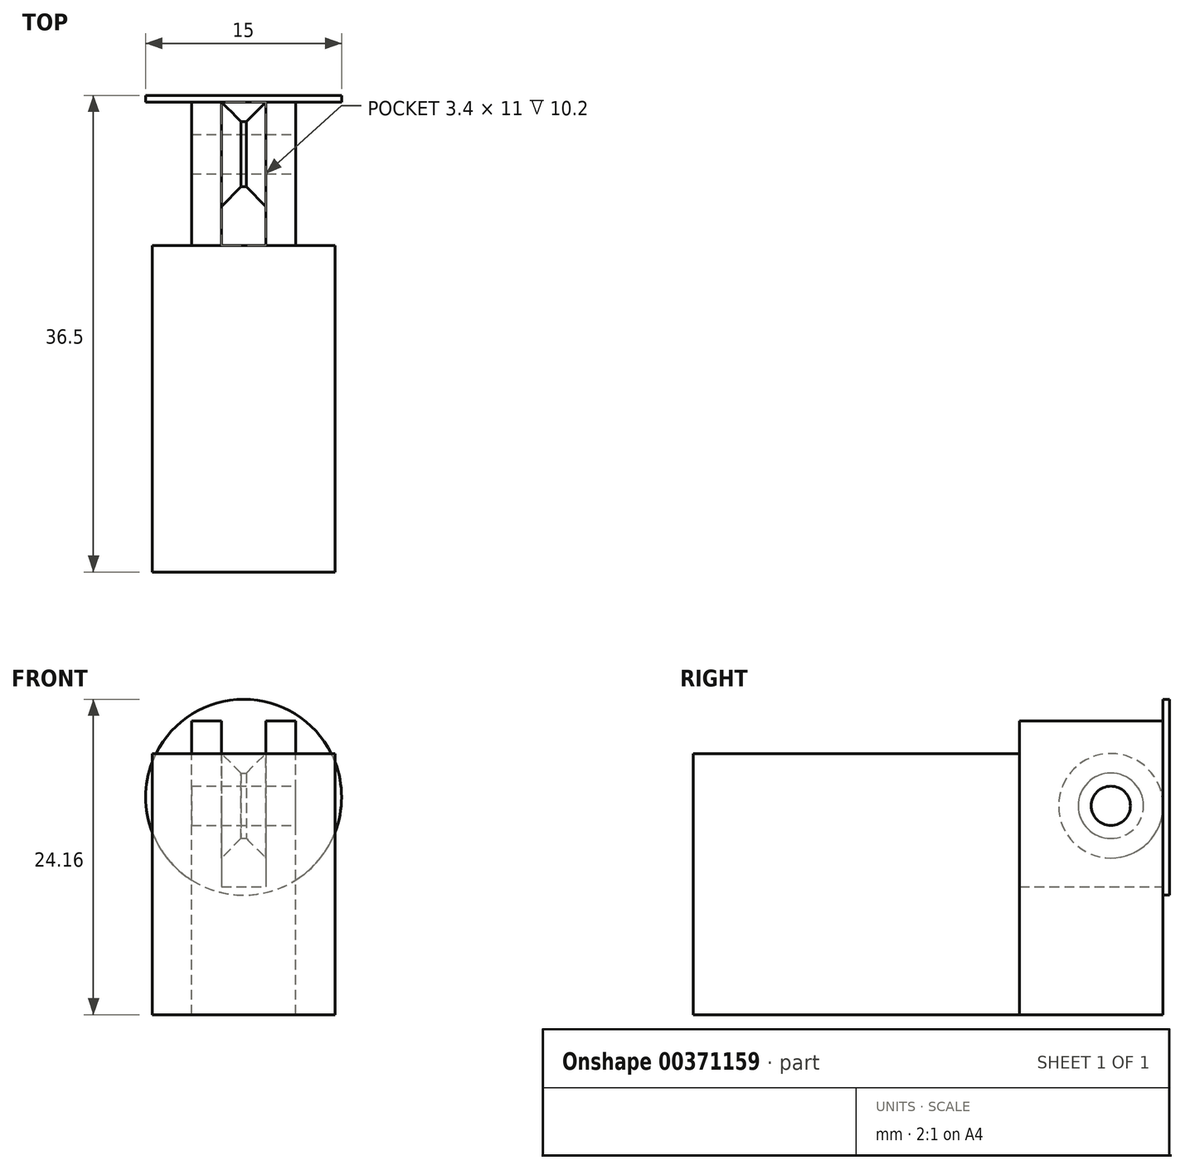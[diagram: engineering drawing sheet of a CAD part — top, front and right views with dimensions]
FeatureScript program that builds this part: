
annotation { "Feature Type Name" : "Feature", "Feature Type Description" : "" }
export const myFeature = defineFeature(function(context is Context, id is Id, definition is map)
    precondition{}
    {
        {
            var Q0;
            Q0=qCreatedBy(makeId("Front.planeOp"),FACE);
            var sketch = newSketch(context, id + "F0", { "sketchPlane" : qUnion([Q0])});
            skLineSegment(sketch, "E0", {"start": v(0, 0) * mm, "end": v(-4, 0) * mm});
            skLineSegment(sketch, "E1", {"start": v(-4, 0) * mm, "end": v(-4, 22.5) * mm});
            skLineSegment(sketch, "E2", {"start": v(-4, 22.5) * mm, "end": v(-1.7, 22.5) * mm});
            skLineSegment(sketch, "E3", {"start": v(-1.7, 22.5) * mm, "end": v(-1.7, 0) * mm, "construction": true});
            skPoint(sketch, "E3.endSnap0", {"position": v(-2, 0) * mm});
            skLineSegment(sketch, "E4", {"start": v(-1.7, 0) * mm, "end": v(-1.7, 9.8) * mm, "construction": true});
            skLineSegment(sketch, "E5", {"start": v(-1.7, 22.5) * mm, "end": v(-1.7, 9.8) * mm});
            skLineSegment(sketch, "E6", {"start": v(-1.7, 9.8) * mm, "end": v(0, 9.8) * mm});
            skLineSegment(sketch, "E7", {"start": v(0, 9.8) * mm, "end": v(0, 0) * mm});
            skCircle(sketch, "E8", {"center": v(0, 9.8) * mm, "radius": 14.4 * mm});
            skSolve(sketch);
        }
        {
            var Q0;
            Q0=makeQuery(id+"F0.imprint","IMPRINT",FACE,{"disambiguationData":[TD([[makeQuery(id+"F0.imprint","IMPRINT",EDGE,{"derivedFrom":sQuery(id+"F0.wireOp",EDGE,"E0")}),-1.0]])]});
            extrude(context, id + "F1", {"entities" : qUnion([Q0]), "depth" : 11 * mm});
        }
        {
            var Q0;
            Q0=makeQuery(id+"F1.opExtrude","SWEPT_BODY",BODY,{"disambiguationData":[OSD([sQuery(id+"F0.wireOp",EDGE,"E0"),sQuery(id+"F0.wireOp",EDGE,"E1"),sQuery(id+"F0.wireOp",EDGE,"E2"),sQuery(id+"F0.wireOp",EDGE,"E5"),sQuery(id+"F0.wireOp",EDGE,"E6"),sQuery(id+"F0.wireOp",EDGE,"E7")])]});
            var Q1;
            Q1=makeQuery(id+"F1.opExtrude","SWEPT_FACE",FACE,{"disambiguationData":[OSD([sQuery(id+"F0.wireOp",EDGE,"E7")])]});
            mirror(context, id + "F2", {"operationType" : NewBodyOperationType.ADD, "entities" : qUnion([Q0]), "mirrorPlane" : qUnion([Q1])});
        }
        {
            var Q0;
            {var subQ0=makeQuery(id+"F1.opExtrude","CAP_FACE",FACE,{"disambiguationData":[OSD([sQuery(id+"F0.wireOp",EDGE,"E0"),sQuery(id+"F0.wireOp",EDGE,"E1"),sQuery(id+"F0.wireOp",EDGE,"E2"),sQuery(id+"F0.wireOp",EDGE,"E5"),sQuery(id+"F0.wireOp",EDGE,"E6"),sQuery(id+"F0.wireOp",EDGE,"E7")])],"isStart":false});Q0=makeQuery(id+"F2.boolean.opBoolean","MERGE",FACE,{"derivedFrom":[subQ0,makeQuery(id+"F2.opPattern","COPY",FACE,{"derivedFrom":subQ0,"instanceName":"1"})]});}
            var sketch = newSketch(context, id + "F3", { "sketchPlane" : qUnion([Q0])});
            skLineSegment(sketch, "E9", {"start": v(0, 0) * mm, "end": v(-7, 0) * mm, "construction": true});
            skLineSegment(sketch, "E10", {"start": v(0, 0) * mm, "end": v(-7, 0) * mm});
            skLineSegment(sketch, "E11", {"start": v(-7, 0) * mm, "end": v(-7, 20) * mm});
            skLineSegment(sketch, "E12", {"start": v(0, 0) * mm, "end": v(7, 0) * mm});
            skLineSegment(sketch, "E13", {"start": v(7, 0) * mm, "end": v(7, 20) * mm});
            skLineSegment(sketch, "E14", {"start": v(-7, 20) * mm, "end": v(7, 20) * mm});
            skSolve(sketch);
        }
        {
            var Q0;
            {var subQ3=sQuery(id+"F3.wireOp",EDGE,"E13");Q0=makeQuery(id+"F3.imprint","IMPRINT",FACE,{"disambiguationData":[TD([[makeQuery(id+"F3.imprint","IMPRINT",EDGE,{"derivedFrom":subQ3}),1.0]])]});}
            var Q1;
            {var subQ13=makeQuery(id+"F1.opExtrude","CAP_EDGE",EDGE,{"disambiguationData":[OSD([sQuery(id+"F0.wireOp",EDGE,"E6")])],"isStart":false});var subQ14=makeQuery(id+"F2.boolean.opBoolean","MERGE",EDGE,{"derivedFrom":[subQ13,makeQuery(id+"F2.opPattern","COPY",EDGE,{"derivedFrom":subQ13,"instanceName":"1"})]});Q1=makeQuery(id+"F3.imprint","IMPRINT",FACE,{"disambiguationData":[TD([[makeQuery(id+"F3.imprint","IMPRINT",EDGE,{"derivedFrom":subQ14}),-1.0]])]});}
            var Q2;
            {var subQ5=makeQuery(id+"F1.opExtrude","CAP_EDGE",EDGE,{"disambiguationData":[OSD([sQuery(id+"F0.wireOp",EDGE,"E6")])],"isStart":false});var subQ6=makeQuery(id+"F2.boolean.opBoolean","MERGE",EDGE,{"derivedFrom":[subQ5,makeQuery(id+"F2.opPattern","COPY",EDGE,{"derivedFrom":subQ5,"instanceName":"1"})]});Q2=makeQuery(id+"F3.imprint","IMPRINT",FACE,{"disambiguationData":[TD([[makeQuery(id+"F3.imprint","IMPRINT",EDGE,{"derivedFrom":subQ6}),1.0]])]});}
            var Q3;
            {var subQ3=sQuery(id+"F3.wireOp",EDGE,"E11");Q3=makeQuery(id+"F3.imprint","IMPRINT",FACE,{"disambiguationData":[TD([[makeQuery(id+"F3.imprint","IMPRINT",EDGE,{"derivedFrom":subQ3}),-1.0]])]});}
            extrude(context, id + "F4", {"entities" : qUnion([Q0, Q1, Q2, Q3]), "operationType" : NewBodyOperationType.ADD, "depth" : 25 * mm});
        }
        {
            var Q0;
            Q0=makeQuery(id+"F2.opPattern","COPY",FACE,{"derivedFrom":makeQuery(id+"F1.opExtrude","SWEPT_FACE",FACE,{"disambiguationData":[OSD([sQuery(id+"F0.wireOp",EDGE,"E1")])]}),"instanceName":"1"});
            var sketch = newSketch(context, id + "F5", { "sketchPlane" : qUnion([Q0])});
            skLineSegment(sketch, "E15", {"start": v(0, 16) * mm, "end": v(-4, 16) * mm, "construction": true});
            skLineSegment(sketch, "E16", {"start": v(-4, 16) * mm, "end": v(-4, 0) * mm, "construction": true});
            skCircle(sketch, "E17", {"center": v(-4, 16) * mm, "radius": 1.5 * mm});
            skCircle(sketch, "E18", {"center": v(-4, 16) * mm, "radius": 2.5 * mm});
            skSolve(sketch);
        }
        {
            var Q0;
            Q0=makeQuery(id+"F5.imprint","IMPRINT",FACE,{"disambiguationData":[TD([[makeQuery(id+"F5.imprint","IMPRINT",EDGE,{"derivedFrom":sQuery(id+"F5.wireOp",EDGE,"E17")}),1.0]])]});
            extrude(context, id + "F6", {"entities" : qUnion([Q0]), "operationType" : NewBodyOperationType.REMOVE, "oppositeDirection" : true, "depth" : 25 * mm});
        }
        {
            var Q0;
            Q0=makeQuery(id+"F5.imprint","IMPRINT",FACE,{"disambiguationData":[TD([[makeQuery(id+"F5.imprint","IMPRINT",EDGE,{"derivedFrom":sQuery(id+"F5.wireOp",EDGE,"E17")}),-1.0]])]});
            var Q1;
            Q1=makeQuery(id+"F1.opExtrude","SWEPT_FACE",FACE,{"disambiguationData":[OSD([sQuery(id+"F0.wireOp",EDGE,"E1")])]});
            extrude(context, id + "F7", {"entities" : qUnion([Q0]), "operationType" : NewBodyOperationType.ADD, "endBound" : BoundingType.UP_TO_SURFACE, "oppositeDirection" : true, "endBoundEntityFace" : qUnion([Q1]), "depth" : 25 * mm});
        }
        {
            var Q0;
            Q0=makeQuery(id+"F7.boolean.opBoolean","INTERSECT",EDGE,{"derivedFrom":[makeQuery(id+"F1.opExtrude","SWEPT_FACE",FACE,{"disambiguationData":[OSD([sQuery(id+"F0.wireOp",EDGE,"E5")])]}),makeQuery(id+"F7.opExtrude","SWEPT_FACE",FACE,{"disambiguationData":[OSD([sQuery(id+"F5.wireOp",EDGE,"E18")])]})]});
            chamfer(context, id + "F8", {"entities" : qUnion([Q0]), "width" : 1.5 * mm, "tangentPropagation" : true});
        }
        {
            var Q0;
            Q0=makeQuery(id+"F7.boolean.opBoolean","INTERSECT",EDGE,{"derivedFrom":[makeQuery(id+"F2.opPattern","COPY",FACE,{"derivedFrom":makeQuery(id+"F1.opExtrude","SWEPT_FACE",FACE,{"disambiguationData":[OSD([sQuery(id+"F0.wireOp",EDGE,"E5")])]}),"instanceName":"1"}),makeQuery(id+"F7.opExtrude","SWEPT_FACE",FACE,{"disambiguationData":[OSD([sQuery(id+"F5.wireOp",EDGE,"E18")])]})]});
            chamfer(context, id + "F9", {"entities" : qUnion([Q0]), "width" : 1.5 * mm, "tangentPropagation" : true});
        }
        {
            var Q0;
            {var subQ0=makeQuery(id+"F1.opExtrude","CAP_FACE",FACE,{"disambiguationData":[OSD([sQuery(id+"F0.wireOp",EDGE,"E0"),sQuery(id+"F0.wireOp",EDGE,"E1"),sQuery(id+"F0.wireOp",EDGE,"E2"),sQuery(id+"F0.wireOp",EDGE,"E5"),sQuery(id+"F0.wireOp",EDGE,"E6"),sQuery(id+"F0.wireOp",EDGE,"E7")])],"isStart":true});Q0=makeQuery(id+"F2.boolean.opBoolean","MERGE",FACE,{"derivedFrom":[subQ0,makeQuery(id+"F2.opPattern","COPY",FACE,{"derivedFrom":subQ0,"instanceName":"1"})]});}
            var sketch = newSketch(context, id + "F10", { "sketchPlane" : qUnion([Q0])});
            skCircle(sketch, "E19", {"center": v(0, 16.66) * mm, "radius": 7.5 * mm});
            skSolve(sketch);
        }
        {
            var Q0;
            Q0=qCreatedBy(makeId("Right.planeOp"),FACE);
            cPlane(context, id + "F11", {"entities" : qUnion([Q0]), "cplaneType" : CPlaneType.OFFSET, "offset" : 25 * mm, "width" : 150 * mm, "height" : 150 * mm});
        }
        {
            var Q0;
            Q0 = qSketchRegion(id + "F10", true);
            extrude(context, id + "F12", {"entities" : qUnion([Q0]), "operationType" : NewBodyOperationType.ADD, "depth" : 0.5 * mm});
        }
    });
